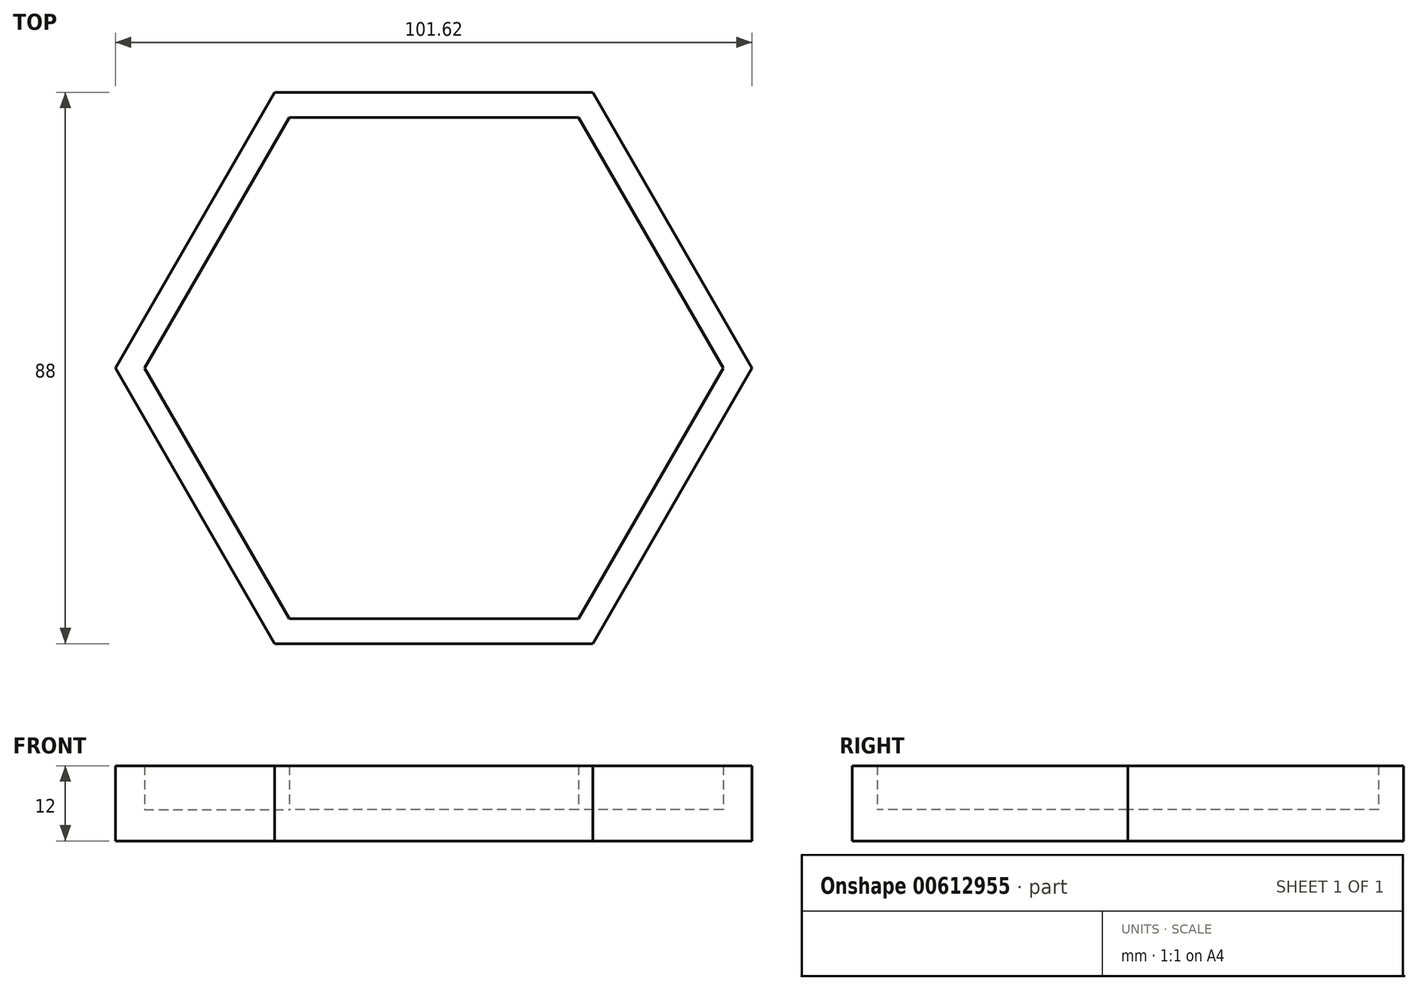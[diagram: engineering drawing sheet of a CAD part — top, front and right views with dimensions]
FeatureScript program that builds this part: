
annotation { "Feature Type Name" : "Feature", "Feature Type Description" : "" }
export const myFeature = defineFeature(function(context is Context, id is Id, definition is map)
    precondition{}
    {
        {
            var Q0;
            Q0=qCreatedBy(makeId("Top.planeOp"),FACE);
            var sketch = newSketch(context, id + "F0", { "sketchPlane" : qUnion([Q0])});
            skCircle(sketch, "E0.cCircle", {"center": v(0, 0) * mm, "radius": 40 * mm, "construction": true});
            skLineSegment(sketch, "E0.0", {"start": v(-46.19, 0) * mm, "end": v(-23.1, 40) * mm});
            skLineSegment(sketch, "E0.1", {"start": v(-23.1, 40) * mm, "end": v(23.1, 40) * mm});
            skLineSegment(sketch, "E0.2", {"start": v(23.1, 40) * mm, "end": v(46.19, 0) * mm});
            skLineSegment(sketch, "E0.3", {"start": v(46.19, 0) * mm, "end": v(23.1, -40) * mm});
            skLineSegment(sketch, "E0.4", {"start": v(23.1, -40) * mm, "end": v(-23.1, -40) * mm});
            skLineSegment(sketch, "E0.5", {"start": v(-23.1, -40) * mm, "end": v(-46.19, 0) * mm});
            skPoint(sketch, "E0.0.midPoint", {"position": v(-34.64, 20) * mm});
            skCircle(sketch, "E1.cCircle", {"center": v(0, 0) * mm, "radius": 44 * mm, "construction": true});
            skLineSegment(sketch, "E1.0", {"start": v(-50.8, 0) * mm, "end": v(-25.4, 44) * mm});
            skLineSegment(sketch, "E1.1", {"start": v(-25.4, 44) * mm, "end": v(25.4, 44) * mm});
            skLineSegment(sketch, "E1.2", {"start": v(25.4, 44) * mm, "end": v(50.8, 0) * mm});
            skLineSegment(sketch, "E1.3", {"start": v(50.8, 0) * mm, "end": v(25.4, -44) * mm});
            skLineSegment(sketch, "E1.4", {"start": v(25.4, -44) * mm, "end": v(-25.4, -44) * mm});
            skLineSegment(sketch, "E1.5", {"start": v(-25.4, -44) * mm, "end": v(-50.8, 0) * mm});
            skPoint(sketch, "E1.0.midPoint", {"position": v(-38.1, 22) * mm});
            skSolve(sketch);
        }
        {
            var Q0;
            Q0=makeQuery(id+"F0.imprint","IMPRINT",FACE,{"disambiguationData":[TD([[makeQuery(id+"F0.imprint","IMPRINT",EDGE,{"derivedFrom":sQuery(id+"F0.wireOp",EDGE,"E0.0")}),-1.0]])]});
            var Q1;
            Q1=makeQuery(id+"F0.imprint","IMPRINT",FACE,{"disambiguationData":[TD([[makeQuery(id+"F0.imprint","IMPRINT",EDGE,{"derivedFrom":sQuery(id+"F0.wireOp",EDGE,"E0.0")}),1.0]])]});
            var Q2;
            Q2=sQuery(id+"F0.wireOp",EDGE,"E0.1");
            var Q3;
            Q3=sQuery(id+"F0.wireOp",EDGE,"E0.0");
            var Q4;
            Q4=sQuery(id+"F0.wireOp",EDGE,"E0.5");
            var Q5;
            Q5=sQuery(id+"F0.wireOp",EDGE,"E0.4");
            var Q6;
            Q6=sQuery(id+"F0.wireOp",EDGE,"E0.3");
            var Q7;
            Q7=sQuery(id+"F0.wireOp",EDGE,"E0.2");
            extrude(context, id + "F1", {"entities" : qUnion([Q0, Q1]), "surfaceEntities" : qUnion([Q2, Q3, Q4, Q5, Q6, Q7]), "depth" : 5 * mm, "offsetDistance" : 25 * mm});
        }
        {
            var Q0;
            Q0=makeQuery(id+"F1.opExtrude","CAP_FACE",FACE,{"disambiguationData":[OSD([sQuery(id+"F0.wireOp",EDGE,"E1.0"),sQuery(id+"F0.wireOp",EDGE,"E1.1"),sQuery(id+"F0.wireOp",EDGE,"E1.2"),sQuery(id+"F0.wireOp",EDGE,"E1.3"),sQuery(id+"F0.wireOp",EDGE,"E1.4"),sQuery(id+"F0.wireOp",EDGE,"E1.5")])],"isStart":false});
            var sketch = newSketch(context, id + "F2", { "sketchPlane" : qUnion([Q0])});
            skLineSegment(sketch, "E2.0.0", {"start": v(-46.19, 0) * mm, "end": v(-23.1, -40) * mm});
            skLineSegment(sketch, "E2.0.1", {"start": v(-23.1, -40) * mm, "end": v(23.1, -40) * mm});
            skLineSegment(sketch, "E2.0.2", {"start": v(23.1, -40) * mm, "end": v(46.19, 0) * mm});
            skLineSegment(sketch, "E2.0.3", {"start": v(46.19, 0) * mm, "end": v(23.1, 40) * mm});
            skLineSegment(sketch, "E2.0.4", {"start": v(23.1, 40) * mm, "end": v(-23.1, 40) * mm});
            skLineSegment(sketch, "E2.0.5", {"start": v(-23.1, 40) * mm, "end": v(-46.19, 0) * mm});
            skLineSegment(sketch, "E3.0.0", {"start": v(-50.8, 0) * mm, "end": v(-25.4, -44) * mm});
            skLineSegment(sketch, "E3.0.1", {"start": v(-25.4, -44) * mm, "end": v(25.4, -44) * mm});
            skLineSegment(sketch, "E3.0.2", {"start": v(25.4, -44) * mm, "end": v(50.8, 0) * mm});
            skLineSegment(sketch, "E3.0.3", {"start": v(50.8, 0) * mm, "end": v(25.4, 44) * mm});
            skLineSegment(sketch, "E3.0.4", {"start": v(25.4, 44) * mm, "end": v(-25.4, 44) * mm});
            skLineSegment(sketch, "E3.0.5", {"start": v(-25.4, 44) * mm, "end": v(-50.8, 0) * mm});
            skSolve(sketch);
        }
        {
            var Q0;
            Q0 = qSketchRegion(id + "F2", true);
            extrude(context, id + "F3", {"entities" : qUnion([Q0]), "operationType" : NewBodyOperationType.ADD, "depth" : 7 * mm, "offsetDistance" : 25 * mm});
        }
    });
